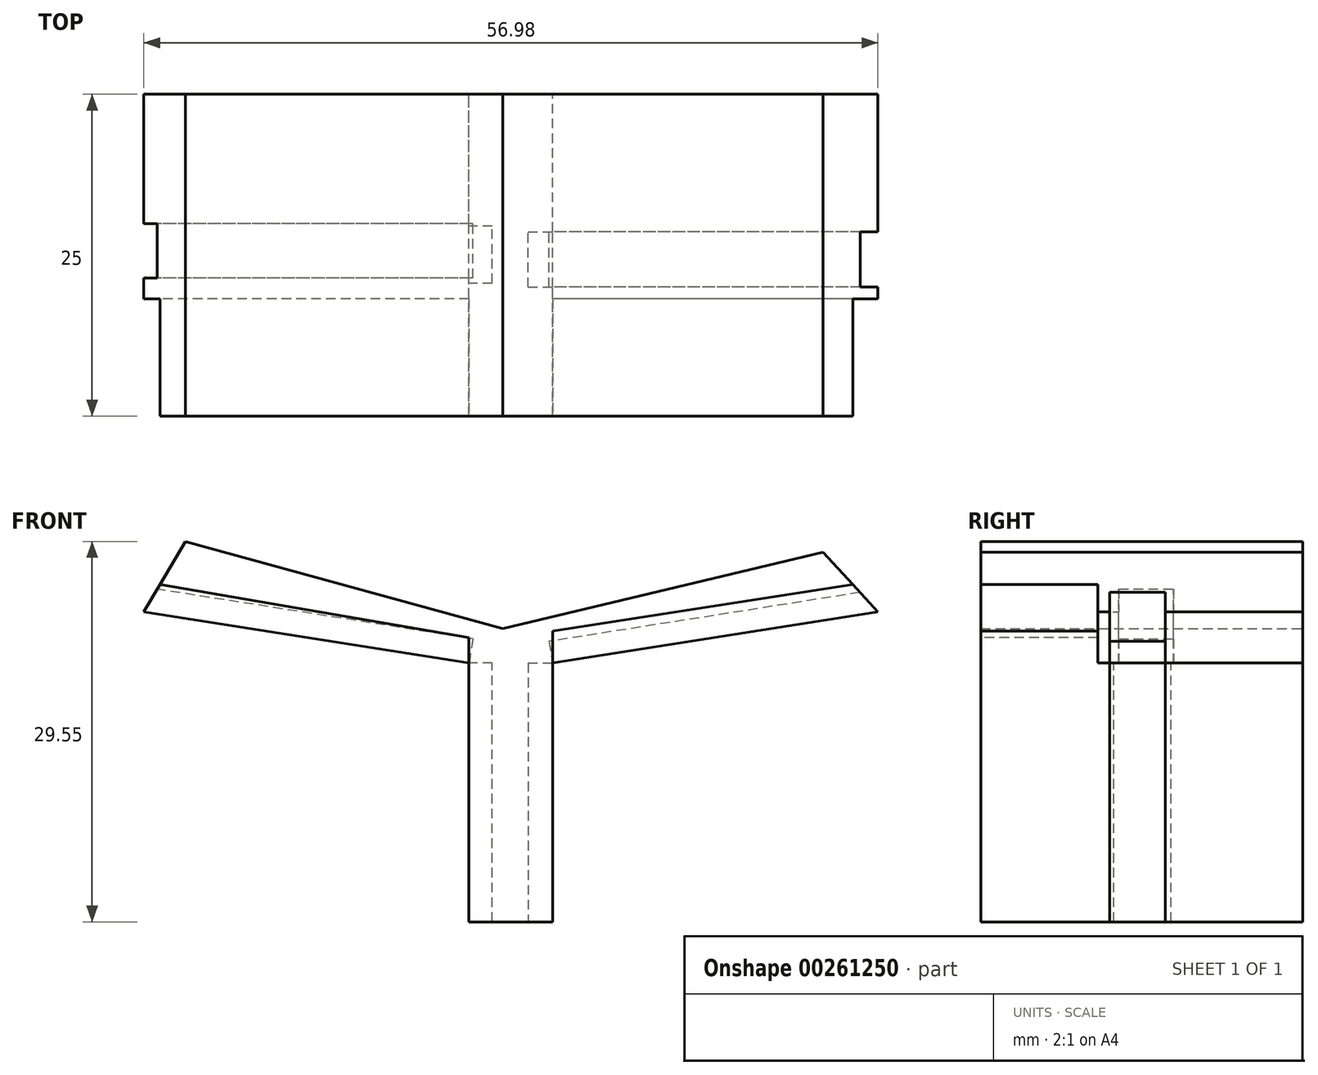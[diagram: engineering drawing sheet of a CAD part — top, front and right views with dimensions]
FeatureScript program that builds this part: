
annotation { "Feature Type Name" : "Feature", "Feature Type Description" : "" }
export const myFeature = defineFeature(function(context is Context, id is Id, definition is map)
    precondition{}
    {
        {
            var Q0;
            Q0=qCreatedBy(makeId("Front.planeOp"),FACE);
            var sketch = newSketch(context, id + "F0", { "sketchPlane" : qUnion([Q0])});
            skLineSegment(sketch, "E0", {"start": v(-44.1, 9.44) * mm, "end": v(-19.46, 2.67) * mm});
            skLineSegment(sketch, "E1", {"start": v(-19.46, 2.67) * mm, "end": v(5.4, 8.63) * mm});
            skLineSegment(sketch, "E2", {"start": v(9.64, 3.98) * mm, "end": v(-15.6, 0) * mm});
            skLineSegment(sketch, "E3", {"start": v(-15.6, 0) * mm, "end": v(-15.6, -20.11) * mm});
            skLineSegment(sketch, "E4", {"start": v(-15.6, -20.11) * mm, "end": v(-22.09, -20.11) * mm});
            skLineSegment(sketch, "E5", {"start": v(-22.09, -20.11) * mm, "end": v(-22.09, 0) * mm});
            skLineSegment(sketch, "E6", {"start": v(-22.09, 0) * mm, "end": v(-47.34, 3.98) * mm});
            skLineSegment(sketch, "E7", {"start": v(5.4, 8.63) * mm, "end": v(9.64, 3.98) * mm});
            skLineSegment(sketch, "E8", {"start": v(-44.1, 9.44) * mm, "end": v(-47.34, 3.98) * mm});
            skSolve(sketch);
        }
        {
            var Q0;
            Q0=makeQuery(id+"F0.imprint","IMPRINT",FACE,{"disambiguationData":[TD([[makeQuery(id+"F0.imprint","IMPRINT",EDGE,{"derivedFrom":sQuery(id+"F0.wireOp",EDGE,"E0")}),-1.0]])]});
            extrude(context, id + "F1", {"entities" : qUnion([Q0]), "depth" : 25 * mm});
        }
        {
            var Q0;
            Q0=makeQuery(id+"F1.opExtrude","SWEPT_FACE",FACE,{"disambiguationData":[OSD([sQuery(id+"F0.wireOp",EDGE,"E2")])]});
            var sketch = newSketch(context, id + "F2", { "sketchPlane" : qUnion([Q0])});
            skLineSegment(sketch, "E9.bottom", {"start": v(10.14, 14.98) * mm, "end": v(-15.41, 14.98) * mm});
            skLineSegment(sketch, "E9.top", {"start": v(10.14, 10.69) * mm, "end": v(-15.41, 10.69) * mm});
            skLineSegment(sketch, "E9.left", {"start": v(10.14, 14.98) * mm, "end": v(10.14, 10.69) * mm});
            skLineSegment(sketch, "E9.right", {"start": v(-15.41, 14.98) * mm, "end": v(-15.41, 10.69) * mm});
            skSolve(sketch);
        }
        {
            var Q0;
            Q0=makeQuery(id+"F2.imprint","IMPRINT",FACE,{"disambiguationData":[TD([[makeQuery(id+"F2.imprint","IMPRINT",EDGE,{"derivedFrom":sQuery(id+"F2.wireOp",EDGE,"E9.bottom")}),1.0]])]});
            extrude(context, id + "F3", {"entities" : qUnion([Q0]), "operationType" : NewBodyOperationType.REMOVE, "oppositeDirection" : true, "depth" : 1.7 * mm});
        }
        {
            var Q0;
            Q0=makeQuery(id+"F1.opExtrude","SWEPT_FACE",FACE,{"disambiguationData":[OSD([sQuery(id+"F0.wireOp",EDGE,"E3")])]});
            var sketch = newSketch(context, id + "F4", { "sketchPlane" : qUnion([Q0])});
            skLineSegment(sketch, "E10.bottom", {"start": v(-10.69, 0) * mm, "end": v(-14.98, 0) * mm});
            skLineSegment(sketch, "E10.top", {"start": v(-10.69, -20.11) * mm, "end": v(-14.98, -20.11) * mm});
            skLineSegment(sketch, "E10.left", {"start": v(-10.69, 0) * mm, "end": v(-10.69, -20.11) * mm});
            skLineSegment(sketch, "E10.right", {"start": v(-14.98, 0) * mm, "end": v(-14.98, -20.11) * mm});
            skSolve(sketch);
        }
        {
            var Q0;
            Q0=makeQuery(id+"F4.imprint","IMPRINT",FACE,{"disambiguationData":[TD([[makeQuery(id+"F4.imprint","IMPRINT",EDGE,{"derivedFrom":sQuery(id+"F4.wireOp",EDGE,"E10.bottom")}),-1.0]])]});
            extrude(context, id + "F5", {"entities" : qUnion([Q0]), "operationType" : NewBodyOperationType.REMOVE, "oppositeDirection" : true, "depth" : 1.9 * mm});
        }
        {
            var Q0;
            Q0=makeQuery(id+"F1.opExtrude","SWEPT_FACE",FACE,{"disambiguationData":[OSD([sQuery(id+"F0.wireOp",EDGE,"E5")])]});
            var sketch = newSketch(context, id + "F6", { "sketchPlane" : qUnion([Q0])});
            skLineSegment(sketch, "E11.bottom", {"start": v(10.25, -20.11) * mm, "end": v(14.7, -20.11) * mm});
            skLineSegment(sketch, "E11.top", {"start": v(10.25, 0) * mm, "end": v(14.7, 0) * mm});
            skLineSegment(sketch, "E11.left", {"start": v(10.25, -20.11) * mm, "end": v(10.25, 0) * mm});
            skLineSegment(sketch, "E11.right", {"start": v(14.7, -20.11) * mm, "end": v(14.7, 0) * mm});
            skSolve(sketch);
        }
        {
            var Q0;
            Q0=makeQuery(id+"F1.opExtrude","SWEPT_FACE",FACE,{"disambiguationData":[OSD([sQuery(id+"F0.wireOp",EDGE,"E6")])]});
            var sketch = newSketch(context, id + "F7", { "sketchPlane" : qUnion([Q0])});
            skLineSegment(sketch, "E12.bottom", {"start": v(-21.82, 10.04) * mm, "end": v(-47.38, 10.04) * mm});
            skLineSegment(sketch, "E12.top", {"start": v(-21.82, 14.29) * mm, "end": v(-47.38, 14.29) * mm});
            skLineSegment(sketch, "E12.left", {"start": v(-21.82, 10.04) * mm, "end": v(-21.82, 14.29) * mm});
            skLineSegment(sketch, "E12.right", {"start": v(-47.38, 10.04) * mm, "end": v(-47.38, 14.29) * mm});
            skSolve(sketch);
        }
        {
            var Q0;
            Q0=makeQuery(id+"F6.imprint","IMPRINT",FACE,{"disambiguationData":[TD([[makeQuery(id+"F6.imprint","IMPRINT",EDGE,{"derivedFrom":sQuery(id+"F6.wireOp",EDGE,"E11.bottom")}),-1.0]])]});
            extrude(context, id + "F8", {"entities" : qUnion([Q0]), "operationType" : NewBodyOperationType.REMOVE, "oppositeDirection" : true, "depth" : 1.8 * mm});
        }
        {
            var Q0;
            Q0=makeQuery(id+"F7.imprint","IMPRINT",FACE,{"disambiguationData":[TD([[makeQuery(id+"F7.imprint","IMPRINT",EDGE,{"derivedFrom":sQuery(id+"F7.wireOp",EDGE,"E12.bottom")}),-1.0]])]});
            extrude(context, id + "F9", {"entities" : qUnion([Q0]), "operationType" : NewBodyOperationType.REMOVE, "oppositeDirection" : true, "depth" : 1.9 * mm});
        }
        {
            var Q0;
            Q0=makeQuery(id+"F1.opExtrude","CAP_FACE",FACE,{"disambiguationData":[OSD([sQuery(id+"F0.wireOp",EDGE,"E0"),sQuery(id+"F0.wireOp",EDGE,"E1"),sQuery(id+"F0.wireOp",EDGE,"E2"),sQuery(id+"F0.wireOp",EDGE,"E3"),sQuery(id+"F0.wireOp",EDGE,"E4"),sQuery(id+"F0.wireOp",EDGE,"E5"),sQuery(id+"F0.wireOp",EDGE,"E6"),sQuery(id+"F0.wireOp",EDGE,"E7"),sQuery(id+"F0.wireOp",EDGE,"E8")])],"isStart":false});
            var sketch = newSketch(context, id + "F10", { "sketchPlane" : qUnion([Q0])});
            skLineSegment(sketch, "E13", {"start": v(8.44, 6.2) * mm, "end": v(-15.6, 2.48) * mm});
            skLineSegment(sketch, "E14", {"start": v(8.44, 6.2) * mm, "end": v(9.64, 3.98) * mm});
            skLineSegment(sketch, "E15", {"start": v(-15.6, 0) * mm, "end": v(9.64, 3.98) * mm});
            skLineSegment(sketch, "E16", {"start": v(-15.6, 2.48) * mm, "end": v(-15.6, 0) * mm});
            skLineSegment(sketch, "E17", {"start": v(-22.09, 0) * mm, "end": v(-22.09, 1.99) * mm});
            skLineSegment(sketch, "E18", {"start": v(-22.09, 1.99) * mm, "end": v(-46.07, 6.11) * mm});
            skLineSegment(sketch, "E19", {"start": v(-46.07, 6.11) * mm, "end": v(-47.34, 3.98) * mm});
            skLineSegment(sketch, "E20", {"start": v(-47.34, 3.98) * mm, "end": v(-22.09, 0) * mm});
            skSolve(sketch);
        }
        {
            var Q0;
            Q0=makeQuery(id+"F10.imprint","IMPRINT",FACE,{"disambiguationData":[TD([[makeQuery(id+"F10.imprint","IMPRINT",EDGE,{"derivedFrom":sQuery(id+"F10.wireOp",EDGE,"E17")}),1.0]])]});
            var Q1;
            {var subQ4=sQuery(id+"F10.wireOp",EDGE,"E15");Q1=makeQuery(id+"F10.imprint","IMPRINT",FACE,{"disambiguationData":[TD([[makeQuery(id+"F10.imprint","IMPRINT",EDGE,{"derivedFrom":subQ4}),-1.0]])]});}
            extrude(context, id + "F11", {"entities" : qUnion([Q0, Q1]), "operationType" : NewBodyOperationType.REMOVE, "oppositeDirection" : true, "depth" : 9.1 * mm});
        }
    });
